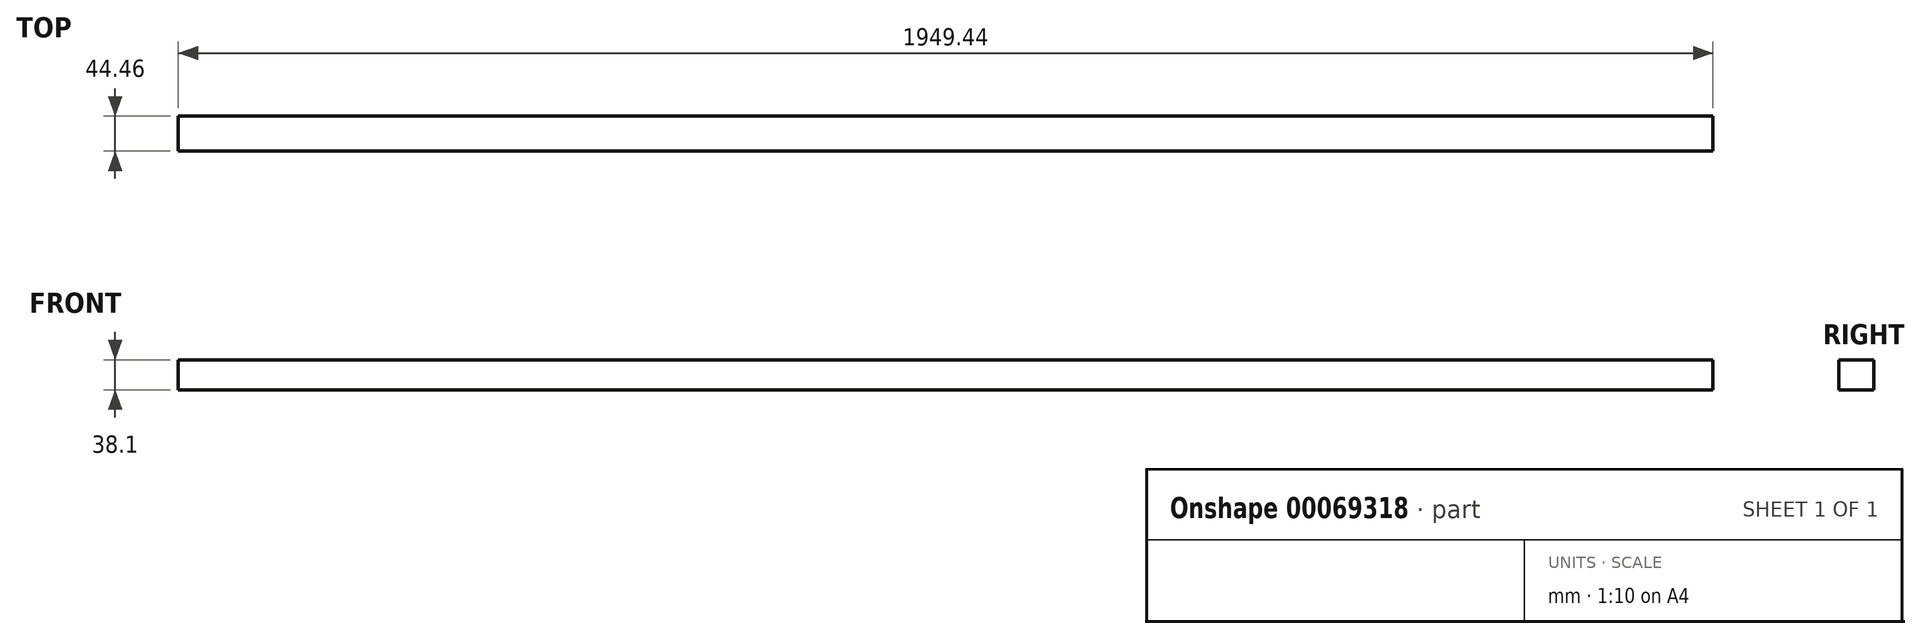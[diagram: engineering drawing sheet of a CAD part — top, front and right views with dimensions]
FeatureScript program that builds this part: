
annotation { "Feature Type Name" : "Feature", "Feature Type Description" : "" }
export const myFeature = defineFeature(function(context is Context, id is Id, definition is map)
    precondition{}
    {
        {
            var Q0;
            Q0=qCreatedBy(makeId("Top.planeOp"),FACE);
            var sketch = newSketch(context, id + "F0", { "sketchPlane" : qUnion([Q0])});
            skLineSegment(sketch, "E0.rect.bottom", {"start": v(-974.73, -22.23) * mm, "end": v(974.73, -22.23) * mm});
            skLineSegment(sketch, "E0.rect.top", {"start": v(-974.73, 22.22) * mm, "end": v(974.73, 22.22) * mm});
            skLineSegment(sketch, "E0.rect.left", {"start": v(-974.73, -22.23) * mm, "end": v(-974.73, 22.22) * mm});
            skLineSegment(sketch, "E0.rect.right", {"start": v(974.73, -22.23) * mm, "end": v(974.73, 22.22) * mm});
            skPoint(sketch, "E0.rect.middle", {"position": v(0, 0) * mm});
            skSolve(sketch);
        }
        {
            var Q0;
            Q0=makeQuery(id+"F0.imprint","IMPRINT",FACE,{"disambiguationData":[TD([[makeQuery(id+"F0.imprint","IMPRINT",EDGE,{"derivedFrom":sQuery(id+"F0.wireOp",EDGE,"E0.rect.bottom")}),1.0]])]});
            extrude(context, id + "F1", {"entities" : qUnion([Q0]), "depth" : 38.1 * mm});
        }
    });
